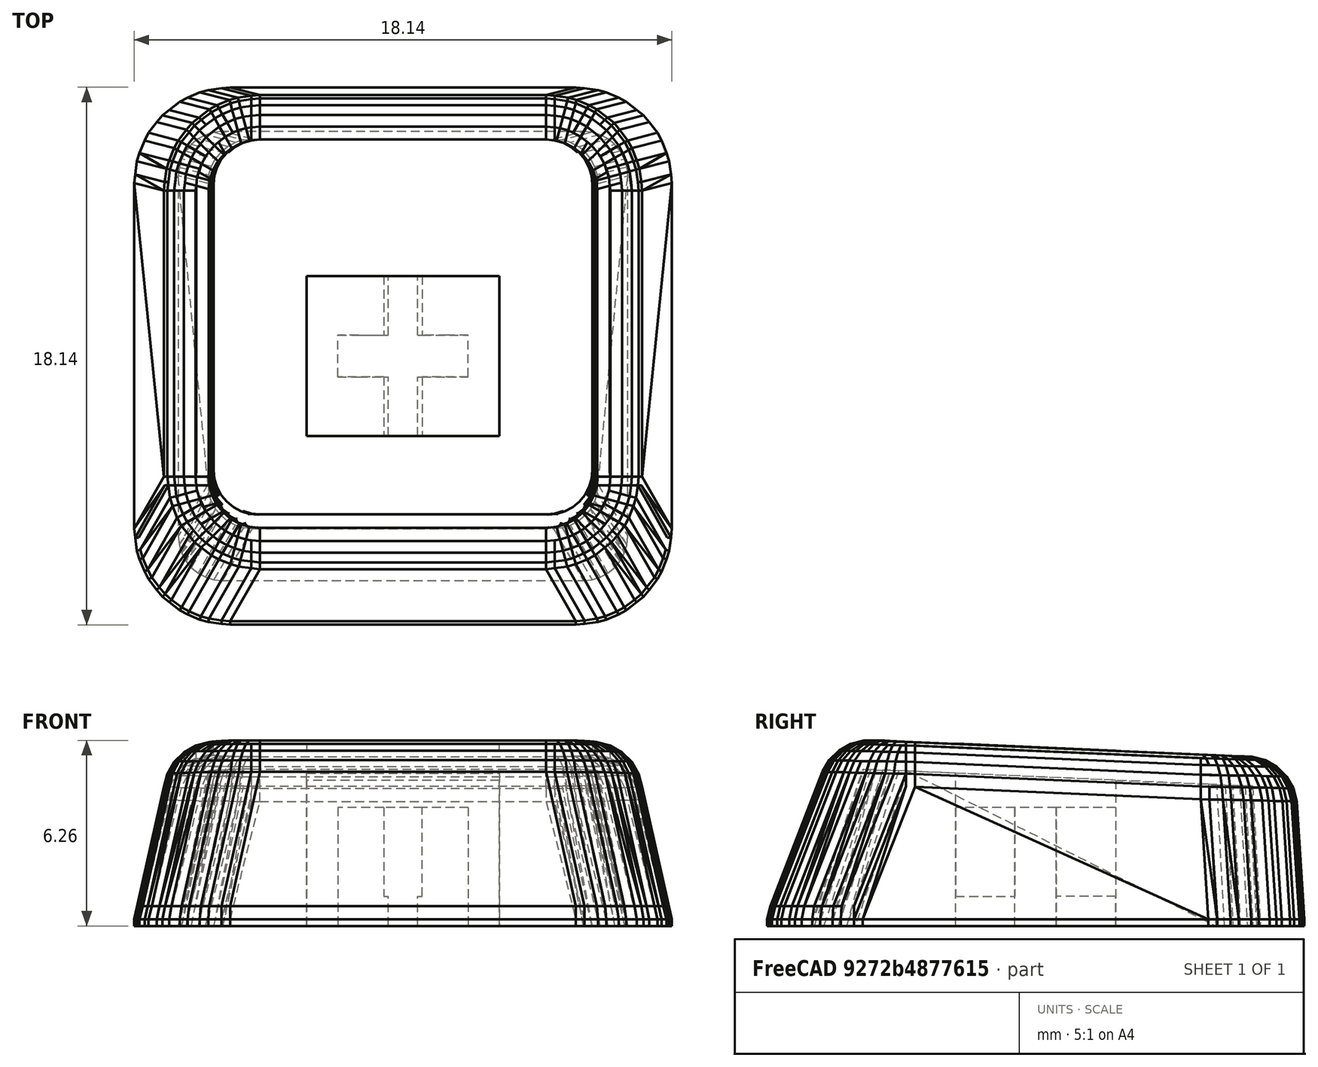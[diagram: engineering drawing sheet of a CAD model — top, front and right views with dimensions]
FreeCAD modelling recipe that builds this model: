
FCSTD DOCUMENT  (FreeCAD 0.18R16131 (Git))
Label: blank
License: All rights reserved
LicenseURL: http://en.wikipedia.org/wiki/All_rights_reserved
objects: Part::Box×4, Part::Feature×1, Part::MultiFuse×1
note: 6 computed .brp shape members not serialized (recipe doc carries the construction recipe); baked Part::Feature solids carry a one-line shape summary decoded from their .brp

FEATURE [Part::Feature] Solid
  shape: bbox 18.13 x 18.13 x 6.262 mm, 1259 faces (baked)
FEATURE [Part::Box] Box  label="Cube"
  AttacherType = Attacher::AttachEngine3D
  Height = 1
  Length = 1
  Placement = pos=(0.5,-2.7,0) rot=(0,0,1;0rad)
  Width = 2
FEATURE [Part::Box] Box001  label="Cube001"
  AttacherType = Attacher::AttachEngine3D
  Height = 1
  Length = 1
  Placement = pos=(-1.5,0.7,0) rot=(0,0,1;0rad)
  Width = 2
FEATURE [Part::Box] Box002  label="Cube002"
  AttacherType = Attacher::AttachEngine3D
  Height = 1
  Length = 1
  Placement = pos=(-1.5,-2.7,0) rot=(0,0,1;0rad)
  Width = 2
FEATURE [Part::Box] Box003  label="Cube003"
  AttacherType = Attacher::AttachEngine3D
  Height = 1
  Length = 1
  Placement = pos=(0.5,0.7,0) rot=(0,0,1;0rad)
  Width = 2
FEATURE [Part::MultiFuse] Fusion
  Shapes = -> [Solid,Box002,Box001,Box,Box003]
